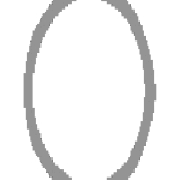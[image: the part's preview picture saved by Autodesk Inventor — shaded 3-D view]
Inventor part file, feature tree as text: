
AUTODESK INVENTOR PART (.ipt)
format: ipt  version: 2021 (Build 250183000, 183)  size: 126,464 bytes
history: native  units: in
note: dims shown in document units (in); Inventor stores cm internally (conversion verified against a paired STEP export)
features: other x4, plane x4, sketch x4, extrude x1, boolean_combine x1
ambient origin geometry x8: Origin, YZ Plane, XZ Plane, XY Plane, X Axis, Y Axis, Z Axis, Center Point
bodies: Solid1 (feature_tree), Body (feature_tree), Solid2 (feature_tree)
feature tree (14):
  other  "Driven Length"
  other  "Frame Generator"
  other  "Start Plane"
  other  "End Plane"
  plane  "Work Plane4"
  plane  "Work Plane5"
  plane  "Work Plane6"
  extrude  "Extrusion3"  Depth=0.065in
  boolean_combine  "Combine1"
  sketch  "Sketch"  dims[d5=37.0212in d6=0.12in d7=0.0in d8=90.0deg d9=37.0212in d10=0.12in d11=0.0in]
  sketch  "Sketch2"  dims[d0=1.0in d1=0.065in]
  plane  "Work Plane3"
  sketch  "Sketch3"  dims[d2=37.0212in]
  sketch  "Sketch4"  dims[d4=-0.0in]
